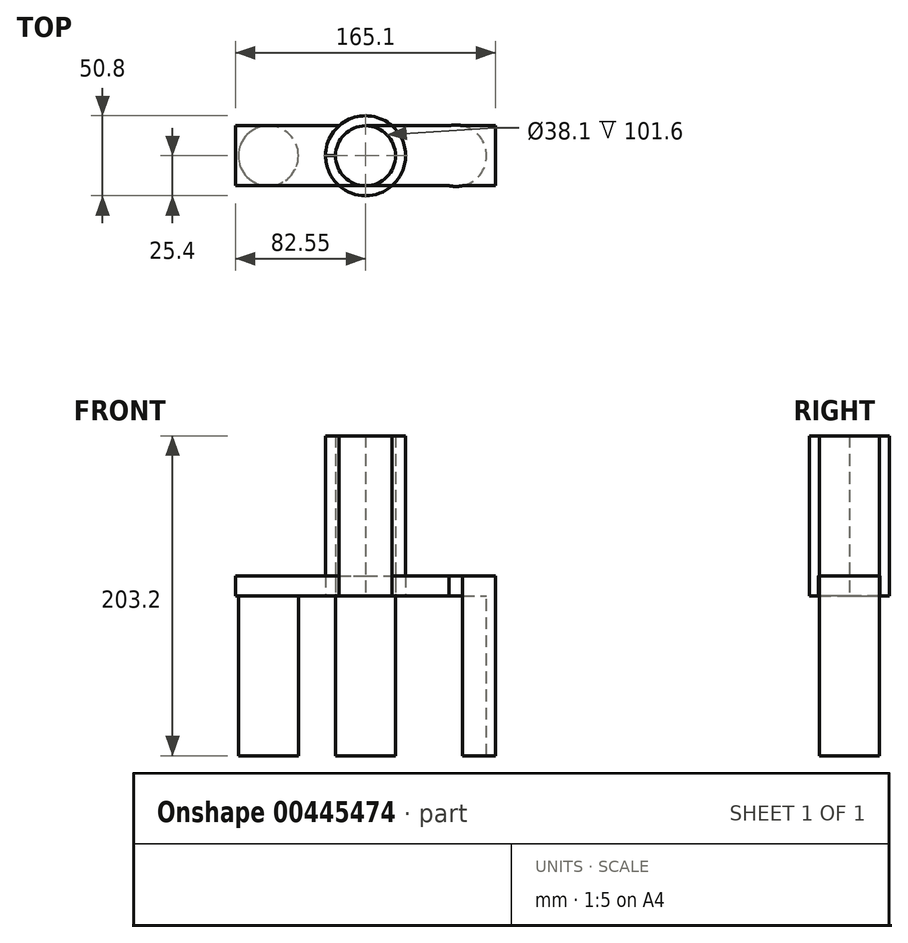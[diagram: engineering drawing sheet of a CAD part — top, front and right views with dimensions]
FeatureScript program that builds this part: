
annotation { "Feature Type Name" : "Feature", "Feature Type Description" : "" }
export const myFeature = defineFeature(function(context is Context, id is Id, definition is map)
    precondition{}
    {
        {
            var Q0;
            Q0=qCreatedBy(makeId("Top.planeOp"),FACE);
            var sketch = newSketch(context, id + "F0", { "sketchPlane" : qUnion([Q0])});
            skLineSegment(sketch, "E0.bottom", {"start": v(-82.55, 19.05) * mm, "end": v(82.55, 19.05) * mm});
            skLineSegment(sketch, "E0.top", {"start": v(-82.55, -19.05) * mm, "end": v(82.55, -19.05) * mm});
            skLineSegment(sketch, "E0.left", {"start": v(-82.55, 19.05) * mm, "end": v(-82.55, -19.05) * mm});
            skLineSegment(sketch, "E0.right", {"start": v(82.55, 19.05) * mm, "end": v(82.55, -19.05) * mm});
            skPoint(sketch, "E0.middle", {"position": v(0, 0) * mm});
            skCircle(sketch, "E1", {"center": v(0, 0) * mm, "radius": 25.4 * mm});
            skCircle(sketch, "E2", {"center": v(0, 0) * mm, "radius": 19.05 * mm});
            skLineSegment(sketch, "E3", {"start": v(-19.05, 0) * mm, "end": v(-44.45, 0) * mm});
            skLineSegment(sketch, "E4", {"start": v(25.4, 0) * mm, "end": v(50.8, 0) * mm});
            skCircle(sketch, "E5", {"center": v(-61.7, 0) * mm, "radius": 19.05 * mm});
            skCircle(sketch, "E6", {"center": v(57.37, 0) * mm, "radius": 19.53 * mm});
            skSolve(sketch);
        }
        {
            var Q0;
            {var subQ0=sQuery(id+"F0.wireOp",EDGE,"E1");var subQ1=sQuery(id+"F0.wireOp",EDGE,"E0.bottom");var subQ2=makeQuery(id+"F0.imprint","INTERSECT",VERTEX,{"disambiguationData":[OD(0.0)],"derivedFrom":[subQ1,subQ0]});Q0=makeQuery(id+"F0.imprint","IMPRINT",FACE,{"disambiguationData":[TD([[makeQuery(id+"F0.imprint","IMPRINT",EDGE,{"disambiguationData":[TD([[subQ2,-1.0]])],"derivedFrom":subQ1}),-1.0]])]});}
            var Q1;
            {var subQ0=sQuery(id+"F0.wireOp",EDGE,"E1");var subQ1=sQuery(id+"F0.wireOp",EDGE,"E0.bottom");var subQ2=makeQuery(id+"F0.imprint","INTERSECT",VERTEX,{"disambiguationData":[OD(0.0)],"derivedFrom":[subQ1,subQ0]});Q1=makeQuery(id+"F0.imprint","IMPRINT",FACE,{"disambiguationData":[TD([[makeQuery(id+"F0.imprint","IMPRINT",EDGE,{"disambiguationData":[TD([[subQ2,-1.0]])],"derivedFrom":subQ1}),1.0]])]});}
            var Q2;
            {var subQ0=sQuery(id+"F0.wireOp",EDGE,"E1");var subQ1=sQuery(id+"F0.wireOp",EDGE,"E0.top");var subQ2=makeQuery(id+"F0.imprint","INTERSECT",VERTEX,{"disambiguationData":[OD(0.0)],"derivedFrom":[subQ1,subQ0]});Q2=makeQuery(id+"F0.imprint","IMPRINT",FACE,{"disambiguationData":[TD([[makeQuery(id+"F0.imprint","IMPRINT",EDGE,{"disambiguationData":[TD([[subQ2,-1.0]])],"derivedFrom":subQ1}),-1.0]])]});}
            extrude(context, id + "F1", {"entities" : qUnion([Q0, Q1, Q2]), "depth" : 101.6 * mm});
        }
        {
            var Q0;
            Q0 = qSketchRegion(id + "F0", true);
            extrude(context, id + "F2", {"entities" : qUnion([Q0]), "operationType" : NewBodyOperationType.ADD, "depth" : 12.7 * mm});
        }
        {
            var Q0;
            {var subQ0=sQuery(id+"F0.wireOp",EDGE,"E5");var subQ1=makeQuery(id+"F0.imprint","INTERSECT",VERTEX,{"derivedFrom":[sQuery(id+"F0.wireOp",EDGE,"E0.bottom"),subQ0]});Q0=makeQuery(id+"F0.imprint","IMPRINT",FACE,{"disambiguationData":[TD([[makeQuery(id+"F0.imprint","IMPRINT",EDGE,{"disambiguationData":[TD([[subQ1,1.0]])],"derivedFrom":subQ0}),1.0]])]});}
            extrude(context, id + "F3", {"entities" : qUnion([Q0]), "operationType" : NewBodyOperationType.ADD, "oppositeDirection" : true, "depth" : 101.6 * mm});
        }
        {
            var Q0;
            {var subQ0=sQuery(id+"F0.wireOp",EDGE,"E2");var subQ1=makeQuery(id+"F0.imprint","INTERSECT",VERTEX,{"derivedFrom":[subQ0,sQuery(id+"F0.wireOp",EDGE,"E3")]});Q0=makeQuery(id+"F0.imprint","IMPRINT",FACE,{"disambiguationData":[TD([[makeQuery(id+"F0.imprint","IMPRINT",EDGE,{"disambiguationData":[TD([[subQ1,1.0]])],"derivedFrom":subQ0}),1.0]])]});}
            extrude(context, id + "F4", {"entities" : qUnion([Q0]), "endBound" : BoundingType.SYMMETRIC, "depth" : 203.2 * mm});
        }
        {
            var Q0;
            {var subQ0=sQuery(id+"F0.wireOp",EDGE,"E6");var subQ4=sQuery(id+"F0.wireOp",EDGE,"E0.bottom");var subQ5=makeQuery(id+"F0.imprint","INTERSECT",VERTEX,{"disambiguationData":[OD(0.0)],"derivedFrom":[subQ4,subQ0]});Q0=makeQuery(id+"F0.imprint","IMPRINT",FACE,{"disambiguationData":[TD([[makeQuery(id+"F0.imprint","IMPRINT",EDGE,{"disambiguationData":[TD([[subQ5,-1.0]])],"derivedFrom":subQ4}),-1.0]])]});}
            extrude(context, id + "F5", {"entities" : qUnion([Q0]), "operationType" : NewBodyOperationType.ADD, "oppositeDirection" : true, "depth" : 101.6 * mm});
        }
        {
            var Q0;
            {var subQ0=sQuery(id+"F0.wireOp",EDGE,"E1");var subQ1=sQuery(id+"F0.wireOp",EDGE,"E0.top");var subQ2=makeQuery(id+"F0.imprint","INTERSECT",VERTEX,{"disambiguationData":[OD(0.0)],"derivedFrom":[subQ1,subQ0]});Q0=makeQuery(id+"F0.imprint","IMPRINT",FACE,{"disambiguationData":[TD([[makeQuery(id+"F0.imprint","IMPRINT",EDGE,{"disambiguationData":[TD([[subQ2,-1.0]])],"derivedFrom":subQ1}),1.0]])]});}
            extrude(context, id + "F6", {"entities" : qUnion([Q0]), "depth" : 101.6 * mm});
        }
        {
            var Q0;
            {var subQ0=sQuery(id+"F0.wireOp",EDGE,"E1");var subQ6=sQuery(id+"F0.wireOp",EDGE,"E0.bottom");var subQ7=makeQuery(id+"F0.imprint","INTERSECT",VERTEX,{"disambiguationData":[OD(1.0)],"derivedFrom":[subQ6,subQ0]});Q0=makeQuery(id+"F0.imprint","IMPRINT",FACE,{"disambiguationData":[TD([[makeQuery(id+"F0.imprint","IMPRINT",EDGE,{"disambiguationData":[TD([[subQ7,1.0]])],"derivedFrom":subQ6}),-1.0]])]});}
            extrude(context, id + "F7", {"entities" : qUnion([Q0]), "depth" : 101.6 * mm});
        }
    });
